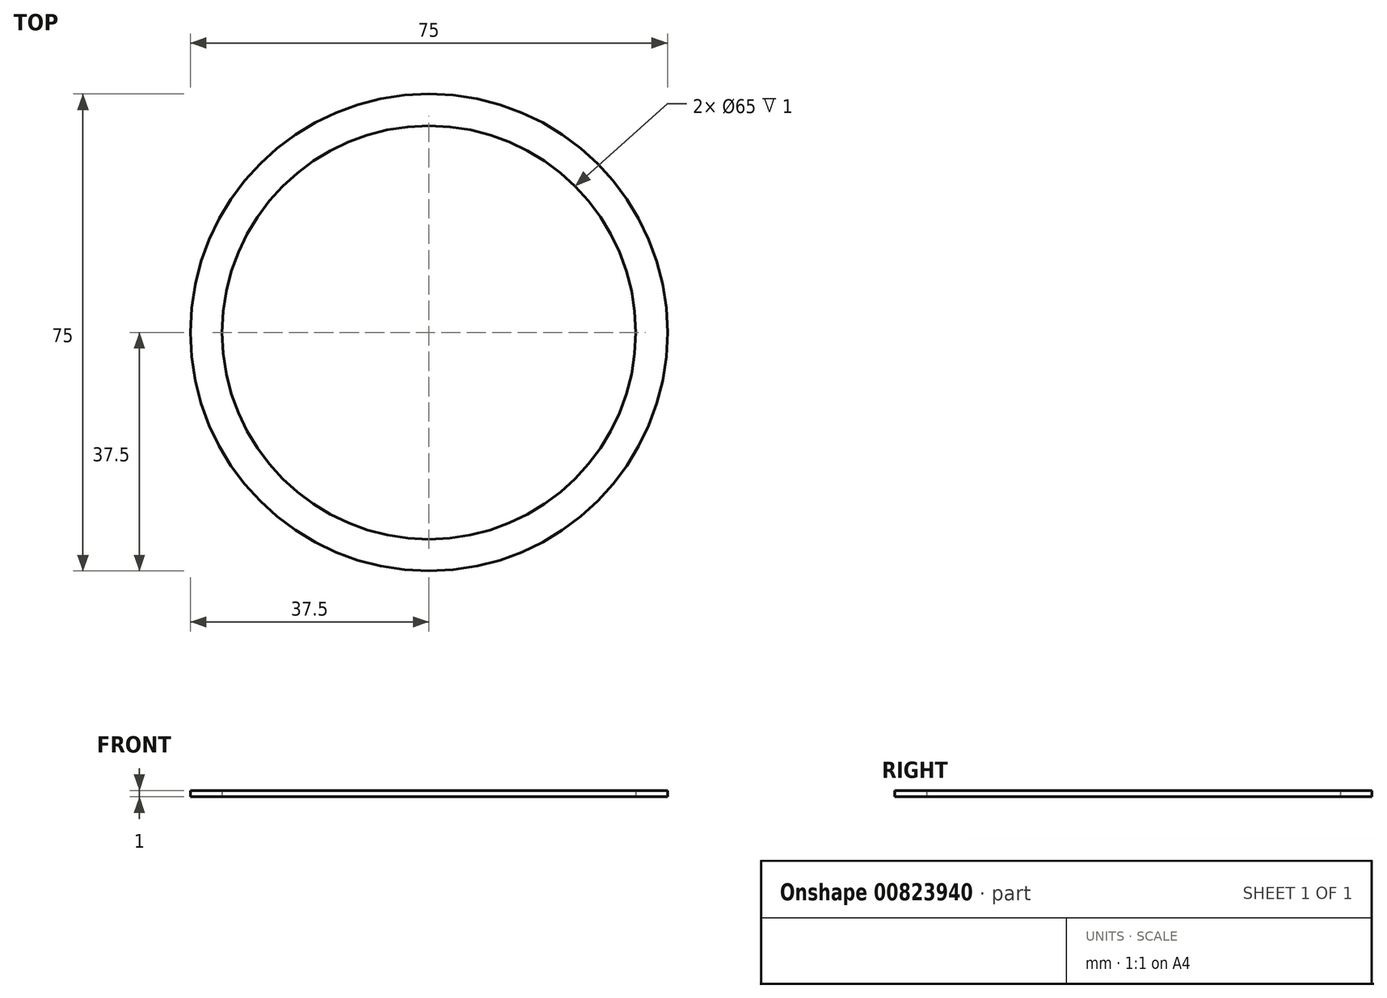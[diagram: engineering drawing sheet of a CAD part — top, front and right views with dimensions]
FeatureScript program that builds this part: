
annotation { "Feature Type Name" : "Feature", "Feature Type Description" : "" }
export const myFeature = defineFeature(function(context is Context, id is Id, definition is map)
    precondition{}
    {
        {
            var Q0;
            Q0=qCreatedBy(makeId("Top.planeOp"),FACE);
            var sketch = newSketch(context, id + "F0", { "sketchPlane" : qUnion([Q0])});
            skCircle(sketch, "E0", {"center": v(0, 0) * mm, "radius": 37.5 * mm});
            skCircle(sketch, "E1", {"center": v(0, 0) * mm, "radius": 32.5 * mm});
            skSolve(sketch);
        }
        {
            var Q0;
            Q0=qSketchRegion(id+"F0",true);
            extrude(context, id + "F1", {"entities" : qUnion([Q0]), "depth" : 1 * mm, "offsetDistance" : 25 * mm});
        }
    });
